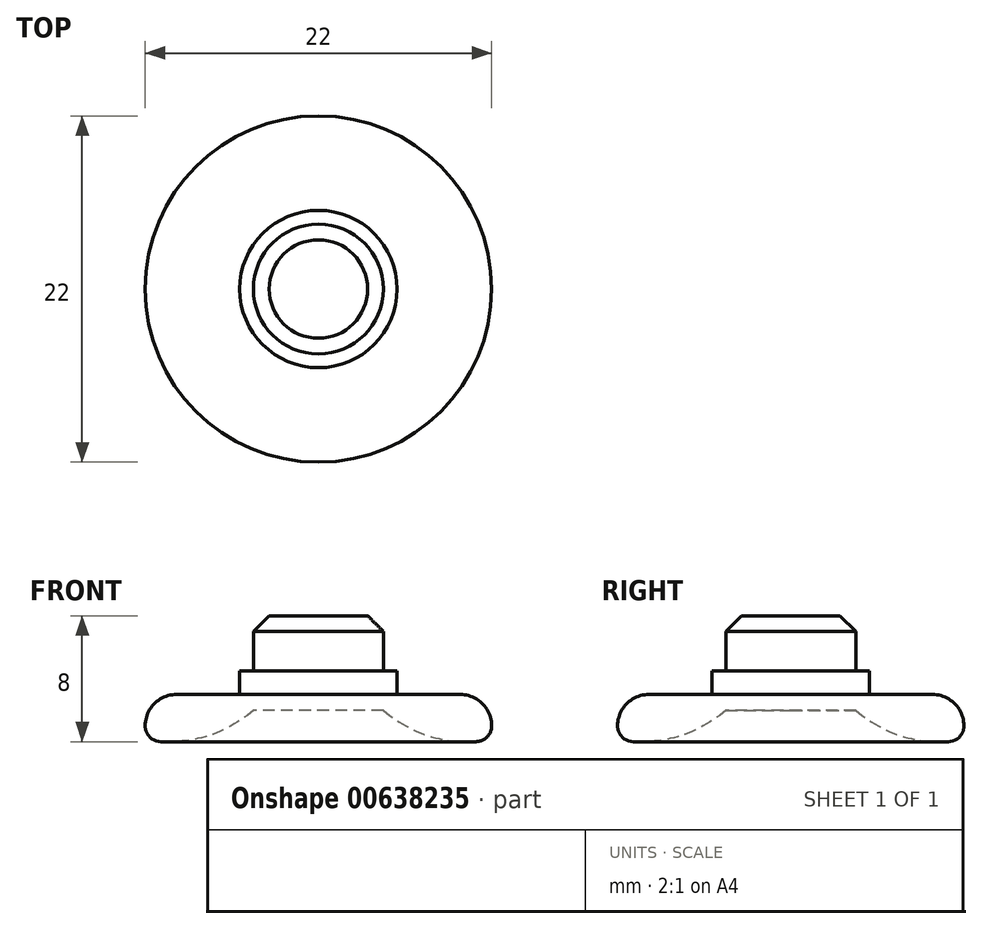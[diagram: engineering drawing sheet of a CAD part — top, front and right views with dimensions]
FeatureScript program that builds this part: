
annotation { "Feature Type Name" : "Feature", "Feature Type Description" : "" }
export const myFeature = defineFeature(function(context is Context, id is Id, definition is map)
    precondition{}
    {
        {
            assignVariable(context, id + "F0", {"name" : "PlateThickness", "anyValue" : 3});
        }
        {
            var Q0;
            Q0=qCreatedBy(makeId("Top.planeOp"),FACE);
            var sketch = newSketch(context, id + "F1", { "sketchPlane" : qUnion([Q0])});
            skCircle(sketch, "E0", {"center": v(0, 0) * mm, "radius": 11 * mm});
            skCircle(sketch, "E1", {"center": v(0, 0) * mm, "radius": 4.12 * mm});
            skCircle(sketch, "E2", {"center": v(0, 0) * mm, "radius": 5 * mm});
            skSolve(sketch);
        }
        {
            var Q0;
            Q0=makeQuery(id+"F1.imprint","IMPRINT",FACE,{"disambiguationData":[TD([[makeQuery(id+"F1.imprint","IMPRINT",EDGE,{"derivedFrom":sQuery(id+"F1.wireOp",EDGE,"E0")}),1.0]])]});
            var Q1;
            Q1=makeQuery(id+"F1.imprint","IMPRINT",FACE,{"disambiguationData":[TD([[makeQuery(id+"F1.imprint","IMPRINT",EDGE,{"derivedFrom":sQuery(id+"F1.wireOp",EDGE,"E1")}),-1.0]])]});
            extrude(context, id + "F2", {"entities" : qUnion([Q0, Q1]), "depth" : (getVariable(context, 'PlateThickness')) * mm, "offsetDistance" : 25 * mm});
        }
        {
            var Q0;
            Q0=makeQuery(id+"F1.imprint","IMPRINT",FACE,{"disambiguationData":[TD([[makeQuery(id+"F1.imprint","IMPRINT",EDGE,{"derivedFrom":sQuery(id+"F1.wireOp",EDGE,"E1")}),1.0]])]});
            extrude(context, id + "F3", {"entities" : qUnion([Q0]), "operationType" : NewBodyOperationType.ADD, "depth" : (getVariable(context, 'PlateThickness') + 5) * mm, "offsetDistance" : 25 * mm, "hasSecondDirection" : true, "secondDirectionOppositeDirection" : false, "secondDirectionDepth" : 2 * mm});
        }
        {
            var Q0;
            Q0=makeQuery(id+"F1.imprint","IMPRINT",FACE,{"disambiguationData":[TD([[makeQuery(id+"F1.imprint","IMPRINT",EDGE,{"derivedFrom":sQuery(id+"F1.wireOp",EDGE,"E1")}),-1.0]])]});
            var Q1;
            Q1=makeQuery(id+"F2.opExtrude","CAP_FACE",FACE,{"disambiguationData":[OSD([sQuery(id+"F1.wireOp",EDGE,"E0"),sQuery(id+"F1.wireOp",EDGE,"E1")])],"isStart":false});
            extrude(context, id + "F4", {"entities" : qUnion([Q0]), "operationType" : NewBodyOperationType.ADD, "depth" : (getVariable(context, 'PlateThickness') + 1.5) * mm, "offsetDistance" : 25 * mm, "hasSecondDirection" : true, "secondDirectionBound" : SecondDirectionBoundingType.UP_TO_SURFACE, "secondDirectionOppositeDirection" : false, "secondDirectionDepth" : 25 * mm, "secondDirectionBoundEntityFace" : qUnion([Q1])});
        }
        {
            var Q0;
            Q0=makeQuery(id+"F3.opExtrude","CAP_EDGE",EDGE,{"disambiguationData":[OSD([sQuery(id+"F1.wireOp",EDGE,"E1")])],"isStart":false});
            chamfer(context, id + "F5", {"entities" : qUnion([Q0]), "width" : 1 * mm, "tangentPropagation" : true});
        }
        {
            var Q0;
            Q0=makeQuery(id+"F2.opExtrude","CAP_EDGE",EDGE,{"disambiguationData":[OSD([sQuery(id+"F1.wireOp",EDGE,"E0")])],"isStart":true});
            fillet(context, id + "F6", {"entities" : qUnion([Q0]), "radius" : 1 * mm, "tangentPropagation" : true, "allowEdgeOverflow" : false});
        }
        {
            var Q0;
            Q0=makeQuery(id+"F2.opExtrude","CAP_EDGE",EDGE,{"disambiguationData":[OSD([sQuery(id+"F1.wireOp",EDGE,"E0")])],"isStart":false});
            fillet(context, id + "F7", {"entities" : qUnion([Q0]), "radius" : 2 * mm, "tangentPropagation" : true, "allowEdgeOverflow" : false});
        }
        {
            var Q0;
            Q0=makeQuery(id+"F2.opExtrude","CAP_EDGE",EDGE,{"disambiguationData":[OSD([sQuery(id+"F1.wireOp",EDGE,"E1")])],"isStart":true});
            fillet(context, id + "F8", {"entities" : qUnion([Q0]), "radius" : 8 * mm, "tangentPropagation" : true, "allowEdgeOverflow" : false});
        }
    });
